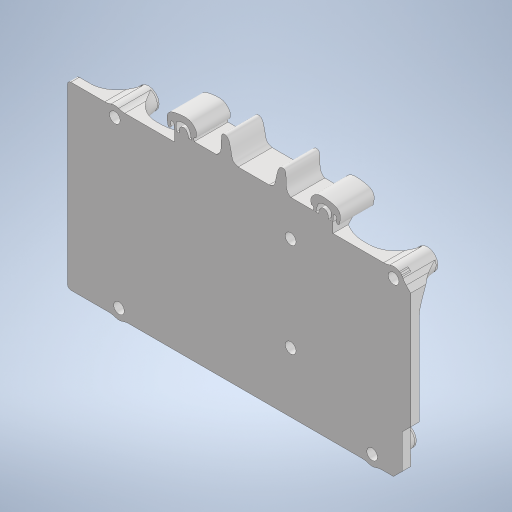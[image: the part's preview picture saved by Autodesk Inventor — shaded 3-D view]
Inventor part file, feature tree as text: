
AUTODESK INVENTOR PART (.ipt)
format: ipt  version: 2023 (Build 270158030, 158C)  size: 596,992 bytes
history: native  units: mm
features: reference x7, other x6, fillet x4, extrude x3, sketch x3
ambient origin geometry x8: Origin, YZ Plane, XZ Plane, XY Plane, X Axis, Y Axis, Z Axis, Center Point
bodies: Body1 (feature_tree)
feature tree (23):
  other  "backplate"
  other  "Blocks"
  extrude  "Extrusion1"  Depth=1.5mm
  extrude  "Extrusion2"  Depth=5.0mm TaperAngle=0.0deg
  fillet  "Fillet2"  Radius=5.0mm
  extrude  "Extrusion3"  Depth=10.0mm TaperAngle=0.0deg
  fillet  "Fillet3"  Radius=7.0mm
  fillet  "Fillet4"  Radius=2.0mm
  fillet  "Fillet5"  Radius=5.0mm
  sketch  "Sketch1"  dims[d0=6.2mm d1=1.5mm]
  reference  "Reference1"
  reference  "Reference2"
  reference  "Reference3"
  reference  "Reference4"
  reference  "Reference5"
  reference  "Reference6"
  sketch  "Sketch2"  dims[d2=10.0mm d3=0.0mm d4=2.5mm d5=0.0mm d7=5.0mm]
  reference  "Reference7"
  sketch  "Sketch3"  dims[d8=23.0mm d9=10.0mm d10=0.0mm d11=7.0mm d12=2.0mm d13=5.0mm]
  other  "din-rail-clip-outline"
  other  "arduino-DIN-mount.iam"
  other  "arduinoMegaDetailed:1"
  other  "din-rail-clip-outline:1"
